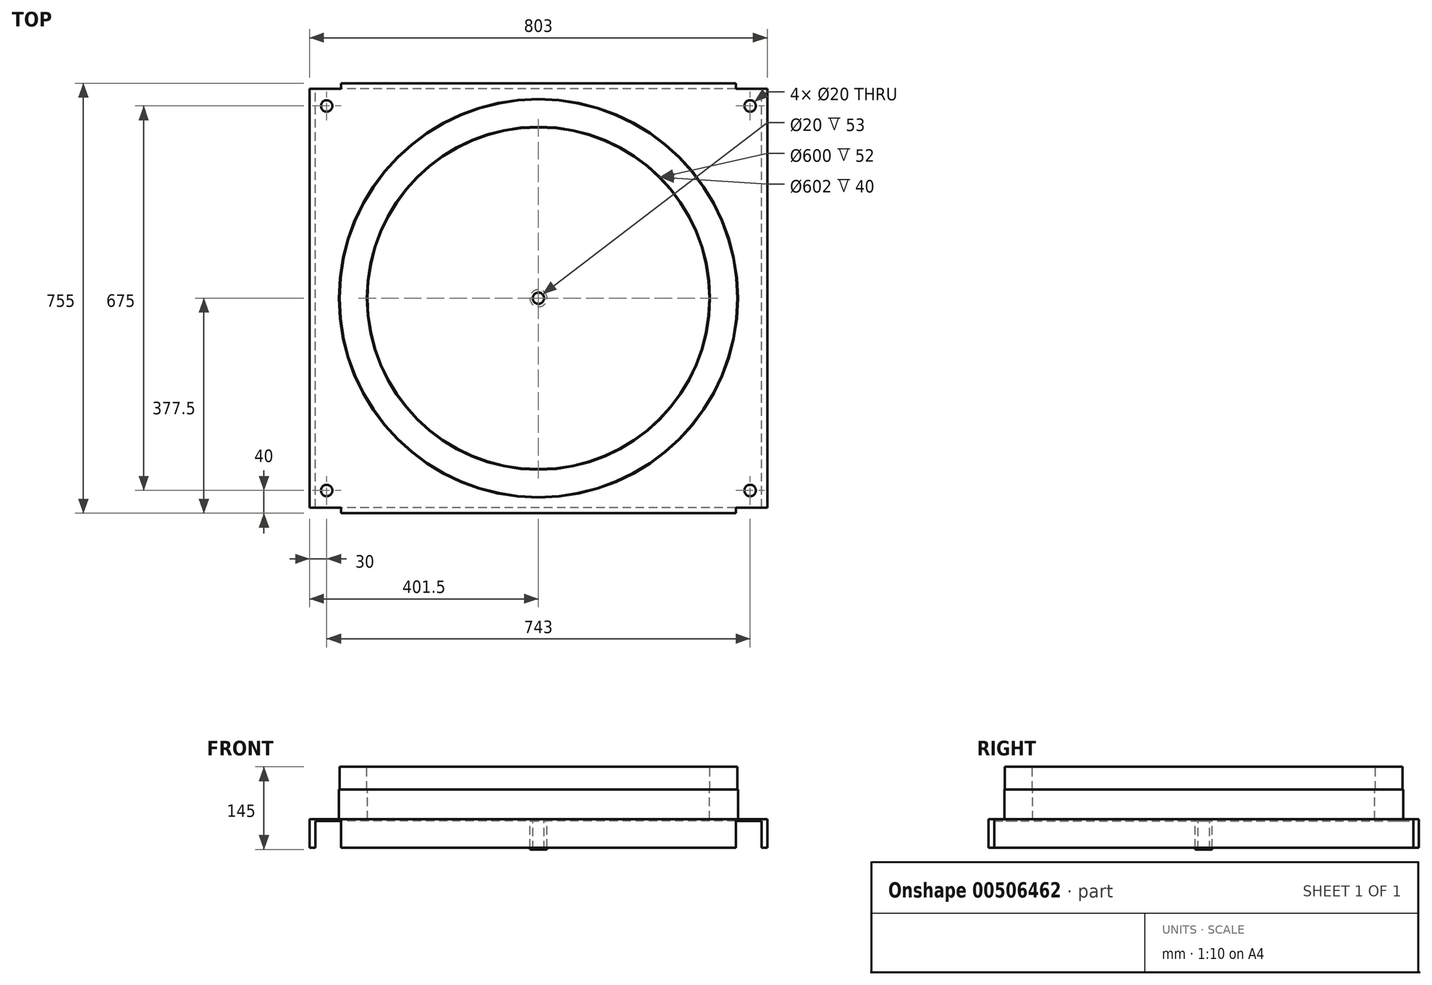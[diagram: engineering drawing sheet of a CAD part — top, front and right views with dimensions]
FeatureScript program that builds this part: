
annotation { "Feature Type Name" : "Feature", "Feature Type Description" : "" }
export const myFeature = defineFeature(function(context is Context, id is Id, definition is map)
    precondition{}
    {
        {
            var Q0;
            Q0=qCreatedBy(makeId("Front.planeOp"),FACE);
            var sketch = newSketch(context, id + "F0", { "sketchPlane" : qUnion([Q0])});
            skLineSegment(sketch, "E0", {"start": v(0, 74.87) * mm, "end": v(0, -73.71) * mm, "construction": true});
            skLineSegment(sketch, "E1", {"start": v(0, 374.84) * mm, "end": v(0, 1) * mm, "construction": true});
            skLineSegment(sketch, "E2", {"start": v(-300, 3) * mm, "end": v(-300, 55) * mm});
            skLineSegment(sketch, "E3", {"start": v(-300, 55) * mm, "end": v(-301, 55) * mm});
            skLineSegment(sketch, "E4", {"start": v(-301, 55) * mm, "end": v(-301, 95) * mm});
            skLineSegment(sketch, "E5", {"start": v(-301, 95) * mm, "end": v(-349, 95) * mm});
            skLineSegment(sketch, "E6", {"start": v(-349, 95) * mm, "end": v(-349, 55) * mm});
            skLineSegment(sketch, "E7", {"start": v(-349, 55) * mm, "end": v(-350, 55) * mm});
            skLineSegment(sketch, "E8", {"start": v(-350, 55) * mm, "end": v(-350, 3) * mm});
            skLineSegment(sketch, "E9", {"start": v(-350, 3) * mm, "end": v(-300, 3) * mm});
            skLineSegment(sketch, "E10.trimOffspring", {"start": v(0, 0) * mm, "end": v(0, -528.94) * mm, "construction": true});
            skLineSegment(sketch, "E11.bottom", {"start": v(-350, 3) * mm, "end": v(-10, 3) * mm});
            skLineSegment(sketch, "E11.top", {"start": v(-350, 0) * mm, "end": v(-10, 0) * mm});
            skLineSegment(sketch, "E11.left", {"start": v(-350, 3) * mm, "end": v(-350, 0) * mm});
            skLineSegment(sketch, "E11.right", {"start": v(-10, 3) * mm, "end": v(-10, 0) * mm});
            skSolve(sketch);
        }
        {
            var Q0;
            Q0=qSketchRegion(id+"F0",true);
            var Q1;
            Q1=sQuery(id+"F0.wireOp",EDGE,"E1");
            revolve(context, id + "F1", {"entities" : qUnion([Q0]), "axis" : qUnion([Q1]), "revolveType" : RevolveType.FULL});
        }
        {
            var Q0;
            Q0=qCreatedBy(makeId("Top.planeOp"),FACE);
            var sketch = newSketch(context, id + "F2", { "sketchPlane" : qUnion([Q0])});
            skLineSegment(sketch, "E12.bottom", {"start": v(401.5, 367.5) * mm, "end": v(-401.5, 367.5) * mm});
            skLineSegment(sketch, "E12.top", {"start": v(401.5, -367.5) * mm, "end": v(-401.5, -367.5) * mm});
            skLineSegment(sketch, "E12.left", {"start": v(401.5, 367.5) * mm, "end": v(401.5, -367.5) * mm});
            skLineSegment(sketch, "E12.right", {"start": v(-401.5, 367.5) * mm, "end": v(-401.5, -367.5) * mm});
            skPoint(sketch, "E12.middle", {"position": v(0, 0) * mm});
            skCircle(sketch, "E13.0", {"center": v(0, 0) * mm, "radius": 301 * mm});
            skCircle(sketch, "E14.0", {"center": v(0, 0) * mm, "radius": 300 * mm});
            skLineSegment(sketch, "E15", {"start": v(0, 0) * mm, "end": v(0, 773.78) * mm, "construction": true});
            skLineSegment(sketch, "E16", {"start": v(0, 0) * mm, "end": v(1007.48, 0) * mm, "construction": true});
            skCircle(sketch, "E17", {"center": v(371.5, 337.5) * mm, "radius": 10 * mm});
            skCircle(sketch, "E18.MirrorC", {"center": v(-371.5, 337.5) * mm, "radius": 10 * mm});
            skCircle(sketch, "E19.MirrorC", {"center": v(371.5, -337.5) * mm, "radius": 10 * mm});
            skCircle(sketch, "E20.MirrorC", {"center": v(-371.5, -337.5) * mm, "radius": 10 * mm});
            skSolve(sketch);
        }
        {
            var Q0;
            Q0=qSketchRegion(id+"F2",true);
            extrude(context, id + "F3", {"entities" : qUnion([Q0]), "operationType" : NewBodyOperationType.ADD, "depth" : 3 * mm, "offsetDistance" : 25 * mm});
        }
        {
            var Q0;
            Q0=makeQuery(id+"F3.opExtrude","CAP_FACE",FACE,{"disambiguationData":[OSD([sQuery(id+"F2.wireOp",EDGE,"E12.bottom"),sQuery(id+"F2.wireOp",EDGE,"E12.top"),sQuery(id+"F2.wireOp",EDGE,"E12.left"),sQuery(id+"F2.wireOp",EDGE,"E12.right"),sQuery(id+"F2.wireOp",EDGE,"E14.0"),sQuery(id+"F2.wireOp",EDGE,"E17"),sQuery(id+"F2.wireOp",EDGE,"E18.MirrorC"),sQuery(id+"F2.wireOp",EDGE,"E19.MirrorC"),sQuery(id+"F2.wireOp",EDGE,"E20.MirrorC")])],"isStart":false});
            var sketch = newSketch(context, id + "F4", { "sketchPlane" : qUnion([Q0])});
            skLineSegment(sketch, "E21", {"start": v(0, 0) * mm, "end": v(-1098.02, 0) * mm, "construction": true});
            skLineSegment(sketch, "E22", {"start": v(0, 0) * mm, "end": v(0, -1084.2) * mm, "construction": true});
            skLineSegment(sketch, "E23.bottom", {"start": v(346.5, -367.5) * mm, "end": v(-346.5, -367.5) * mm});
            skLineSegment(sketch, "E23.top", {"start": v(346.5, -377.5) * mm, "end": v(-346.5, -377.5) * mm});
            skLineSegment(sketch, "E23.left", {"start": v(346.5, -367.5) * mm, "end": v(346.5, -377.5) * mm});
            skLineSegment(sketch, "E23.right", {"start": v(-346.5, -367.5) * mm, "end": v(-346.5, -377.5) * mm});
            skLineSegment(sketch, "E24.bottom", {"start": v(-401.5, -367.5) * mm, "end": v(-391.5, -367.5) * mm});
            skLineSegment(sketch, "E24.top", {"start": v(-401.5, 367.5) * mm, "end": v(-391.5, 367.5) * mm});
            skLineSegment(sketch, "E24.left", {"start": v(-401.5, 367.5) * mm, "end": v(-401.5, -367.5) * mm});
            skLineSegment(sketch, "E24.right", {"start": v(-391.5, 367.5) * mm, "end": v(-391.5, -367.5) * mm});
            skLineSegment(sketch, "E25.MirrorCS", {"start": v(346.5, 367.5) * mm, "end": v(346.5, 377.5) * mm});
            skLineSegment(sketch, "E26.MirrorCS", {"start": v(-346.5, 367.5) * mm, "end": v(-346.5, 377.5) * mm});
            skLineSegment(sketch, "E27.MirrorCS", {"start": v(346.5, 377.5) * mm, "end": v(-346.5, 377.5) * mm});
            skLineSegment(sketch, "E28.MirrorCS", {"start": v(346.5, 367.5) * mm, "end": v(-346.5, 367.5) * mm});
            skLineSegment(sketch, "E29.MirrorCS", {"start": v(401.5, 367.5) * mm, "end": v(391.5, 367.5) * mm});
            skLineSegment(sketch, "E30.MirrorCS", {"start": v(401.5, -367.5) * mm, "end": v(391.5, -367.5) * mm});
            skLineSegment(sketch, "E31.MirrorCS", {"start": v(401.5, 367.5) * mm, "end": v(401.5, -367.5) * mm});
            skLineSegment(sketch, "E32.MirrorCS", {"start": v(391.5, 367.5) * mm, "end": v(391.5, -367.5) * mm});
            skLineSegment(sketch, "E33.MirrorCS", {"start": v(0, 0) * mm, "end": v(1098.02, 0) * mm, "construction": true});
            skSolve(sketch);
        }
        {
            var Q0;
            Q0=qSketchRegion(id+"F4",true);
            extrude(context, id + "F5", {"entities" : qUnion([Q0]), "operationType" : NewBodyOperationType.ADD, "oppositeDirection" : true, "depth" : 50 * mm, "offsetDistance" : 25 * mm});
        }
        {
            var Q0;
            Q0=makeQuery(id+"F3.boolean.opBoolean","MERGE",FACE,{"derivedFrom":[makeQuery(id+"F1.opRevolve","SWEPT_FACE",FACE,{"disambiguationData":[OSD([sQuery(id+"F0.wireOp",EDGE,"E11.top")])]}),makeQuery(id+"F3.opExtrude","CAP_FACE",FACE,{"disambiguationData":[OSD([sQuery(id+"F2.wireOp",EDGE,"E12.bottom"),sQuery(id+"F2.wireOp",EDGE,"E12.top"),sQuery(id+"F2.wireOp",EDGE,"E12.left"),sQuery(id+"F2.wireOp",EDGE,"E12.right"),sQuery(id+"F2.wireOp",EDGE,"E13.0"),sQuery(id+"F2.wireOp",EDGE,"E17"),sQuery(id+"F2.wireOp",EDGE,"E18.MirrorC"),sQuery(id+"F2.wireOp",EDGE,"E19.MirrorC"),sQuery(id+"F2.wireOp",EDGE,"E20.MirrorC")])],"isStart":false})]});
            var sketch = newSketch(context, id + "F6", { "sketchPlane" : qUnion([Q0])});
            skCircle(sketch, "E34.0", {"center": v(0, 0) * mm, "radius": 10 * mm});
            skCircle(sketch, "E35", {"center": v(0, 0) * mm, "radius": 15 * mm});
            skSolve(sketch);
        }
        {
            var Q0;
            Q0=qSketchRegion(id+"F6",true);
            extrude(context, id + "F7", {"entities" : qUnion([Q0]), "operationType" : NewBodyOperationType.ADD, "depth" : 50 * mm, "offsetDistance" : 25 * mm});
        }
    });
